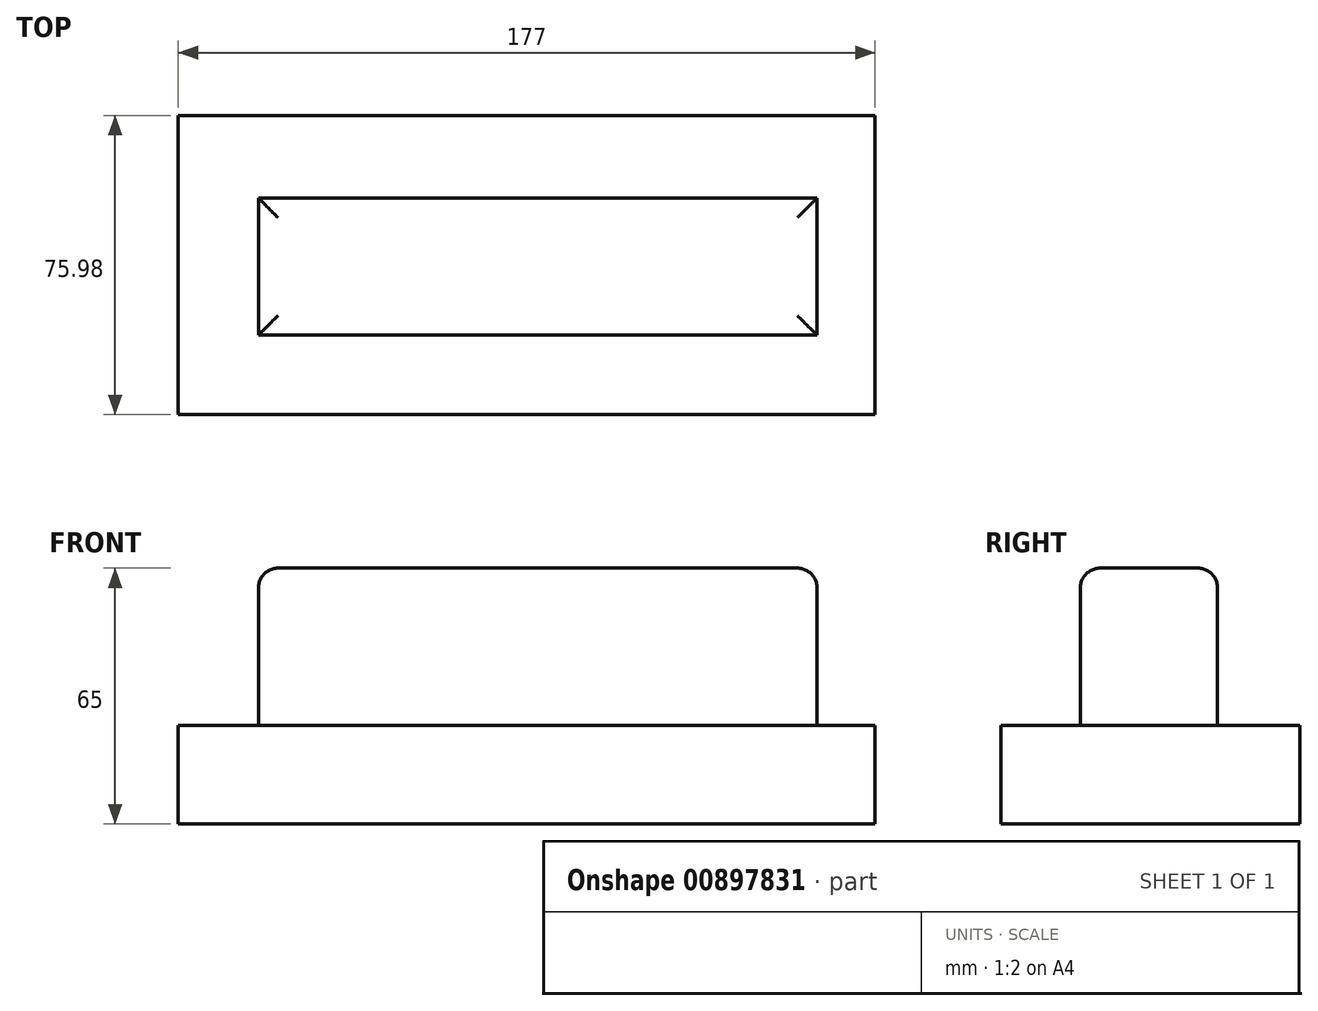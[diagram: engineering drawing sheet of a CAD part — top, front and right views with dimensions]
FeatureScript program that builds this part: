
annotation { "Feature Type Name" : "Feature", "Feature Type Description" : "" }
export const myFeature = defineFeature(function(context is Context, id is Id, definition is map)
    precondition{}
    {
        {
            var Q0;
            Q0=qCreatedBy(makeId("Top.planeOp"),FACE);
            var sketch = newSketch(context, id + "F0", { "sketchPlane" : qUnion([Q0])});
            skLineSegment(sketch, "E0.bottom", {"start": v(-86.77, 34.97) * mm, "end": v(90.23, 34.97) * mm});
            skLineSegment(sketch, "E0.top", {"start": v(-86.77, -41.01) * mm, "end": v(90.23, -41.01) * mm});
            skLineSegment(sketch, "E0.left", {"start": v(-86.77, 34.97) * mm, "end": v(-86.77, -41.01) * mm});
            skLineSegment(sketch, "E0.right", {"start": v(90.23, 34.97) * mm, "end": v(90.23, -41.01) * mm});
            skSolve(sketch);
        }
        {
            var Q0;
            Q0=makeQuery(id+"F0.imprint","IMPRINT",FACE,{"disambiguationData":[TD([[makeQuery(id+"F0.imprint","IMPRINT",EDGE,{"derivedFrom":sQuery(id+"F0.wireOp",EDGE,"E0.bottom")}),-1.0]])]});
            extrude(context, id + "F1", {"entities" : qUnion([Q0]), "depth" : 25 * mm, "offsetDistance" : 25 * mm});
        }
        {
            var Q0;
            Q0=makeQuery(id+"F1.opExtrude","CAP_FACE",FACE,{"disambiguationData":[OSD([sQuery(id+"F0.wireOp",EDGE,"E0.bottom"),sQuery(id+"F0.wireOp",EDGE,"E0.top"),sQuery(id+"F0.wireOp",EDGE,"E0.left"),sQuery(id+"F0.wireOp",EDGE,"E0.right")])],"isStart":false});
            var sketch = newSketch(context, id + "F2", { "sketchPlane" : qUnion([Q0])});
            skLineSegment(sketch, "E1.bottom", {"start": v(-66.4, 14.02) * mm, "end": v(75.52, 14.02) * mm});
            skLineSegment(sketch, "E1.top", {"start": v(-66.4, -20.82) * mm, "end": v(75.52, -20.82) * mm});
            skLineSegment(sketch, "E1.left", {"start": v(-66.4, 14.02) * mm, "end": v(-66.4, -20.82) * mm});
            skLineSegment(sketch, "E1.right", {"start": v(75.52, 14.02) * mm, "end": v(75.52, -20.82) * mm});
            skSolve(sketch);
        }
        {
            var Q0;
            Q0=makeQuery(id+"F2.imprint","IMPRINT",FACE,{"disambiguationData":[TD([[makeQuery(id+"F2.imprint","IMPRINT",EDGE,{"derivedFrom":sQuery(id+"F2.wireOp",EDGE,"E1.bottom")}),-1.0]])]});
            extrude(context, id + "F3", {"entities" : qUnion([Q0]), "operationType" : NewBodyOperationType.ADD, "depth" : 40 * mm, "offsetDistance" : 25 * mm});
        }
        {
            var Q0;
            Q0=makeQuery(id+"F3.opExtrude","CAP_EDGE",EDGE,{"disambiguationData":[OSD([sQuery(id+"F2.wireOp",EDGE,"E1.top")])],"isStart":false});
            var Q1;
            Q1=makeQuery(id+"F3.opExtrude","CAP_EDGE",EDGE,{"disambiguationData":[OSD([sQuery(id+"F2.wireOp",EDGE,"E1.left")])],"isStart":false});
            var Q2;
            Q2=makeQuery(id+"F3.opExtrude","CAP_EDGE",EDGE,{"disambiguationData":[OSD([sQuery(id+"F2.wireOp",EDGE,"E1.bottom")])],"isStart":false});
            var Q3;
            Q3=makeQuery(id+"F3.opExtrude","CAP_EDGE",EDGE,{"disambiguationData":[OSD([sQuery(id+"F2.wireOp",EDGE,"E1.right")])],"isStart":false});
            fillet(context, id + "F4", {"entities" : qUnion([Q0, Q1, Q2, Q3]), "radius" : 5 * mm, "tangentPropagation" : true, "allowEdgeOverflow" : false});
        }
    });
